# Revit family: 3000 Björk Handdryer
name_source: partatom
category: Furniture Systems
revit_build: Autodesk Revit 2017 (Build: 20160720_1515(x64)
units: mm (PartAtom-declared; Revit-internal decimal feet)

## family parameters
Always vertical = Yes
Cut with Voids When Loaded = No
Host = Wall
Part Type = Normal
Room Calculation Point = No
Round Connector Dimension = Use Diameter
Shared = No

## types (6) — shared parameters
Description = Touch-free hand dryer
Manufacturer = Dan Dryer
Model = Björk-3000
Surface Front = WHITE
Type Image = <None>
zero-valued in all types: Cost

## per-type parameters (varying)
| type | URL |
| BIRK | http://www.dandryer.dk |
| GEO WHITE | http://www.dandryer.dk |
| GRIGIO LONDRA | http://www.dandryer.dk |
| NEGRO INGO | http://www.dandryer.dk |
| OSLO | http://www.dandryer.com |
| BIANCO MALE | http://www.dandryer.dk |

note: column(s) folded — value = type name in every type: Surface Top

## geometry (parser evidence)
native form markers: Sweep x4
no freeform markers — native parametric forms only
